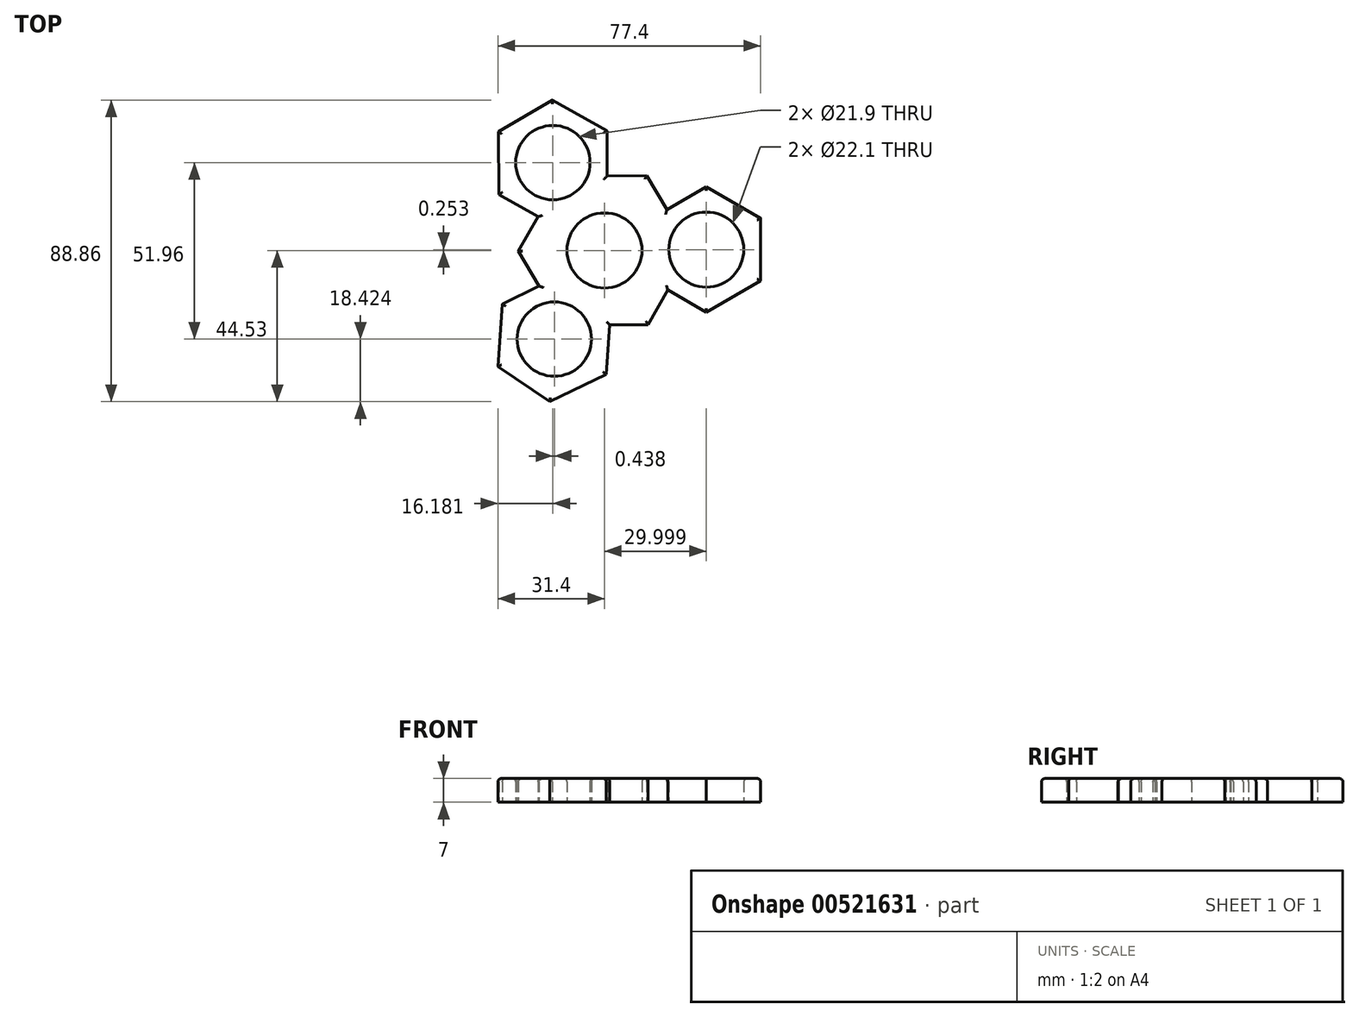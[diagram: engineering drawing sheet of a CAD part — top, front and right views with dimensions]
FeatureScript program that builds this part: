
annotation { "Feature Type Name" : "Feature", "Feature Type Description" : "" }
export const myFeature = defineFeature(function(context is Context, id is Id, definition is map)
    precondition{}
    {
        {
            var Q0;
            Q0=qCreatedBy(makeId("Top.planeOp"),FACE);
            var sketch = newSketch(context, id + "F0", { "sketchPlane" : qUnion([Q0])});
            skCircle(sketch, "E0", {"center": v(0, 0) * mm, "radius": 11.05 * mm});
            skCircle(sketch, "E1", {"center": v(-15.22, 25.85) * mm, "radius": 10.95 * mm});
            skCircle(sketch, "E2", {"center": v(-14.78, -26.1) * mm, "radius": 10.95 * mm});
            skCircle(sketch, "E3", {"center": v(30, 0.25) * mm, "radius": 11.05 * mm});
            skPoint(sketch, "E4.0.midPoint", {"position": v(5.37, -17.18) * mm});
            skPoint(sketch, "E5.0.midPoint", {"position": v(-24.47, 12.8) * mm});
            skLineSegment(sketch, "E6.0", {"start": v(-13.47, -7.68) * mm, "end": v(1.84, -18.03) * mm});
            skLineSegment(sketch, "E6.1", {"start": v(1.84, -18.03) * mm, "end": v(0.52, -36.46) * mm});
            skLineSegment(sketch, "E6.2", {"start": v(0.52, -36.46) * mm, "end": v(-16.1, -44.53) * mm});
            skLineSegment(sketch, "E6.3", {"start": v(-16.1, -44.53) * mm, "end": v(-31.4, -34.18) * mm});
            skLineSegment(sketch, "E6.4", {"start": v(-31.4, -34.18) * mm, "end": v(-30.08, -15.76) * mm});
            skLineSegment(sketch, "E6.5", {"start": v(-30.08, -15.76) * mm, "end": v(-13.47, -7.68) * mm});
            skPoint(sketch, "E6.0.midPoint", {"position": v(-5.82, -12.85) * mm});
            skLineSegment(sketch, "E7.0", {"start": v(14, -8.98) * mm, "end": v(14, 9.5) * mm});
            skLineSegment(sketch, "E7.1", {"start": v(14, 9.5) * mm, "end": v(30, 18.73) * mm});
            skLineSegment(sketch, "E7.2", {"start": v(30, 18.73) * mm, "end": v(46, 9.5) * mm});
            skLineSegment(sketch, "E7.3", {"start": v(46, 9.5) * mm, "end": v(46, -8.98) * mm});
            skLineSegment(sketch, "E7.4", {"start": v(46, -8.98) * mm, "end": v(30, -18.22) * mm});
            skLineSegment(sketch, "E7.5", {"start": v(30, -18.22) * mm, "end": v(14, -8.98) * mm});
            skPoint(sketch, "E7.0.midPoint", {"position": v(14, 0.25) * mm});
            skLineSegment(sketch, "E8.0", {"start": v(0.86, 16.75) * mm, "end": v(-15.06, 7.38) * mm});
            skLineSegment(sketch, "E8.1", {"start": v(-15.06, 7.38) * mm, "end": v(-31.14, 16.48) * mm});
            skLineSegment(sketch, "E8.2", {"start": v(-31.14, 16.48) * mm, "end": v(-31.3, 34.96) * mm});
            skLineSegment(sketch, "E8.3", {"start": v(-31.3, 34.96) * mm, "end": v(-15.37, 44.33) * mm});
            skLineSegment(sketch, "E8.4", {"start": v(-15.37, 44.33) * mm, "end": v(0.7, 35.23) * mm});
            skLineSegment(sketch, "E8.5", {"start": v(0.7, 35.23) * mm, "end": v(0.86, 16.75) * mm});
            skPoint(sketch, "E8.0.midPoint", {"position": v(-7.1, 12.06) * mm});
            skPoint(sketch, "E9.0.midPoint", {"position": v(-15.06, 7.38) * mm});
            skLineSegment(sketch, "E10", {"start": v(0, 0) * mm, "end": v(-15.22, 25.85) * mm});
            skLineSegment(sketch, "E11", {"start": v(0, 0) * mm, "end": v(-14.78, -26.1) * mm});
            skLineSegment(sketch, "E12", {"start": v(0, 0) * mm, "end": v(30, 0.25) * mm});
            skCircle(sketch, "E13.cCircle", {"center": v(0, 0) * mm, "radius": 21.95 * mm, "construction": true});
            skLineSegment(sketch, "E13.0", {"start": v(-12.86, 21.85) * mm, "end": v(12.49, 22.06) * mm});
            skLineSegment(sketch, "E13.1", {"start": v(12.49, 22.06) * mm, "end": v(25.35, 0.21) * mm});
            skLineSegment(sketch, "E13.2", {"start": v(25.35, 0.21) * mm, "end": v(12.86, -21.85) * mm});
            skLineSegment(sketch, "E13.3", {"start": v(12.86, -21.85) * mm, "end": v(-12.49, -22.06) * mm});
            skLineSegment(sketch, "E13.4", {"start": v(-12.49, -22.06) * mm, "end": v(-25.35, -0.21) * mm});
            skLineSegment(sketch, "E13.5", {"start": v(-25.35, -0.21) * mm, "end": v(-12.86, 21.85) * mm});
            skPoint(sketch, "E13.0.midPoint", {"position": v(-0.19, 21.95) * mm});
            skSolve(sketch);
        }
        {
            var Q0;
            {var subQ0=sQuery(id+"F0.wireOp",EDGE,"e9zcL3uG-clMW-CB6R-mPn1-NTrwoYadkIhf");var subQ1=sQuery(id+"F0.wireOp",EDGE,"E0");var subQ2=makeQuery(id+"F0.imprint","INTERSECT",VERTEX,{"derivedFrom":[subQ1,subQ0]});Q0=makeQuery(id+"F0.imprint","IMPRINT",FACE,{"disambiguationData":[TD([[makeQuery(id+"F0.imprint","IMPRINT",EDGE,{"disambiguationData":[TD([[subQ2,-1.0]])],"derivedFrom":subQ1}),-1.0]])]});}
            var Q1;
            Q1=makeQuery(id+"F0.imprint","IMPRINT",FACE,{"disambiguationData":[TD([[makeQuery(id+"F0.imprint","IMPRINT",EDGE,{"derivedFrom":sQuery(id+"F0.wireOp",EDGE,"E2")}),-1.0]])]});
            var Q2;
            {var subQ0=sQuery(id+"F0.wireOp",EDGE,"fM1NJ59R-5Gtm-2Vz8-hERX-S4Y3RQeVmU9U");var subQ1=sQuery(id+"F0.wireOp",EDGE,"EYICjCoY-6TXZ-VuYl-5S1G-jobRDzOFtBTO");var subQ2=makeQuery(id+"F0.imprint","INTERSECT",VERTEX,{"derivedFrom":[subQ1,subQ0]});Q2=makeQuery(id+"F0.imprint","IMPRINT",FACE,{"disambiguationData":[TD([[makeQuery(id+"F0.imprint","IMPRINT",EDGE,{"disambiguationData":[TD([[subQ2,-1.0]])],"derivedFrom":subQ1}),-1.0]])]});}
            var Q3;
            {var subQ0=sQuery(id+"F0.wireOp",EDGE,"oOAs71K8-LSWc-4CLp-Zzfn-c75iS4tNiohm");var subQ1=sQuery(id+"F0.wireOp",EDGE,"E0");var subQ2=makeQuery(id+"F0.imprint","INTERSECT",VERTEX,{"derivedFrom":[subQ1,subQ0]});Q3=makeQuery(id+"F0.imprint","IMPRINT",FACE,{"disambiguationData":[TD([[makeQuery(id+"F0.imprint","IMPRINT",EDGE,{"disambiguationData":[TD([[subQ2,1.0]])],"derivedFrom":subQ1}),-1.0]])]});}
            var Q4;
            {var subQ1=sQuery(id+"F0.wireOp",EDGE,"EYICjCoY-6TXZ-VuYl-5S1G-jobRDzOFtBTO");var subQ3=sQuery(id+"F0.wireOp",EDGE,"jgwlEjWp-sw9u-VY17-f9nH-SewB5XZ8HkPX");var subQ4=makeQuery(id+"F0.imprint","INTERSECT",VERTEX,{"derivedFrom":[subQ1,subQ3]});Q4=makeQuery(id+"F0.imprint","IMPRINT",FACE,{"disambiguationData":[TD([[makeQuery(id+"F0.imprint","IMPRINT",EDGE,{"disambiguationData":[TD([[subQ4,1.0]])],"derivedFrom":subQ3}),1.0]])]});}
            var Q5;
            {var subQ0=sQuery(id+"F0.wireOp",EDGE,"e9zcL3uG-clMW-CB6R-mPn1-NTrwoYadkIhf");var subQ1=sQuery(id+"F0.wireOp",EDGE,"E0");var subQ2=makeQuery(id+"F0.imprint","INTERSECT",VERTEX,{"derivedFrom":[subQ1,subQ0]});Q5=makeQuery(id+"F0.imprint","IMPRINT",FACE,{"disambiguationData":[TD([[makeQuery(id+"F0.imprint","IMPRINT",EDGE,{"disambiguationData":[TD([[subQ2,1.0]])],"derivedFrom":subQ1}),-1.0]])]});}
            var Q6;
            {var subQ1=sQuery(id+"F0.wireOp",EDGE,"EYICjCoY-6TXZ-VuYl-5S1G-jobRDzOFtBTO");var subQ3=sQuery(id+"F0.wireOp",EDGE,"oOAs71K8-LSWc-4CLp-Zzfn-c75iS4tNiohm");var subQ4=makeQuery(id+"F0.imprint","INTERSECT",VERTEX,{"derivedFrom":[subQ1,subQ3]});Q6=makeQuery(id+"F0.imprint","IMPRINT",FACE,{"disambiguationData":[TD([[makeQuery(id+"F0.imprint","IMPRINT",EDGE,{"disambiguationData":[TD([[subQ4,1.0]])],"derivedFrom":subQ3}),1.0]])]});}
            var Q7;
            Q7=makeQuery(id+"F0.imprint","IMPRINT",FACE,{"disambiguationData":[TD([[makeQuery(id+"F0.imprint","IMPRINT",EDGE,{"derivedFrom":sQuery(id+"F0.wireOp",EDGE,"E3")}),-1.0]])]});
            var Q8;
            Q8=makeQuery(id+"F0.imprint","IMPRINT",FACE,{"disambiguationData":[TD([[makeQuery(id+"F0.imprint","IMPRINT",EDGE,{"derivedFrom":sQuery(id+"F0.wireOp",EDGE,"E1")}),-1.0]])]});
            var Q9;
            {var subQ0=sQuery(id+"F0.wireOp",EDGE,"iWpcJYMW-lp7D-Rta9-vDUY-uTJnxPVIUKOB");var subQ1=sQuery(id+"F0.wireOp",EDGE,"EYICjCoY-6TXZ-VuYl-5S1G-jobRDzOFtBTO");var subQ2=makeQuery(id+"F0.imprint","INTERSECT",VERTEX,{"derivedFrom":[subQ1,subQ0]});Q9=makeQuery(id+"F0.imprint","IMPRINT",FACE,{"disambiguationData":[TD([[makeQuery(id+"F0.imprint","IMPRINT",EDGE,{"disambiguationData":[TD([[subQ2,-1.0]])],"derivedFrom":subQ1}),-1.0]])]});}
            var Q10;
            {var subQ0=sQuery(id+"F0.wireOp",EDGE,"nEZrQKPM-t3Dd-AM5R-DWg6-JUV7cxrYPtug");var subQ1=sQuery(id+"F0.wireOp",EDGE,"EYICjCoY-6TXZ-VuYl-5S1G-jobRDzOFtBTO");var subQ2=makeQuery(id+"F0.imprint","INTERSECT",VERTEX,{"derivedFrom":[subQ1,subQ0]});Q10=makeQuery(id+"F0.imprint","IMPRINT",FACE,{"disambiguationData":[TD([[makeQuery(id+"F0.imprint","IMPRINT",EDGE,{"disambiguationData":[TD([[subQ2,-1.0]])],"derivedFrom":subQ1}),-1.0]])]});}
            var Q11;
            {var subQ0=sQuery(id+"F0.wireOp",EDGE,"oOAs71K8-LSWc-4CLp-Zzfn-c75iS4tNiohm");var subQ1=sQuery(id+"F0.wireOp",EDGE,"EYICjCoY-6TXZ-VuYl-5S1G-jobRDzOFtBTO");var subQ2=makeQuery(id+"F0.imprint","INTERSECT",VERTEX,{"derivedFrom":[subQ1,subQ0]});Q11=makeQuery(id+"F0.imprint","IMPRINT",FACE,{"disambiguationData":[TD([[makeQuery(id+"F0.imprint","IMPRINT",EDGE,{"disambiguationData":[TD([[subQ2,1.0]])],"derivedFrom":subQ1}),1.0]])]});}
            var Q12;
            {var subQ0=sQuery(id+"F0.wireOp",EDGE,"jgwlEjWp-sw9u-VY17-f9nH-SewB5XZ8HkPX");var subQ1=sQuery(id+"F0.wireOp",EDGE,"EYICjCoY-6TXZ-VuYl-5S1G-jobRDzOFtBTO");var subQ2=makeQuery(id+"F0.imprint","INTERSECT",VERTEX,{"derivedFrom":[subQ1,subQ0]});Q12=makeQuery(id+"F0.imprint","IMPRINT",FACE,{"disambiguationData":[TD([[makeQuery(id+"F0.imprint","IMPRINT",EDGE,{"disambiguationData":[TD([[subQ2,1.0]])],"derivedFrom":subQ1}),1.0]])]});}
            var Q13;
            {var subQ1=sQuery(id+"F0.wireOp",EDGE,"EYICjCoY-6TXZ-VuYl-5S1G-jobRDzOFtBTO");var subQ3=sQuery(id+"F0.wireOp",EDGE,"e9zcL3uG-clMW-CB6R-mPn1-NTrwoYadkIhf");var subQ4=makeQuery(id+"F0.imprint","INTERSECT",VERTEX,{"derivedFrom":[subQ1,subQ3]});Q13=makeQuery(id+"F0.imprint","IMPRINT",FACE,{"disambiguationData":[TD([[makeQuery(id+"F0.imprint","IMPRINT",EDGE,{"disambiguationData":[TD([[subQ4,1.0]])],"derivedFrom":subQ3}),1.0]])]});}
            var Q14;
            {var subQ0=sQuery(id+"F0.wireOp",EDGE,"e9zcL3uG-clMW-CB6R-mPn1-NTrwoYadkIhf");var subQ1=sQuery(id+"F0.wireOp",EDGE,"EYICjCoY-6TXZ-VuYl-5S1G-jobRDzOFtBTO");var subQ2=makeQuery(id+"F0.imprint","INTERSECT",VERTEX,{"derivedFrom":[subQ1,subQ0]});Q14=makeQuery(id+"F0.imprint","IMPRINT",FACE,{"disambiguationData":[TD([[makeQuery(id+"F0.imprint","IMPRINT",EDGE,{"disambiguationData":[TD([[subQ2,1.0]])],"derivedFrom":subQ1}),1.0]])]});}
            var Q15;
            {var subQ0=sQuery(id+"F0.wireOp",EDGE,"z9qJ6aSi-ppxI-sIG3-XNC9-JwUbkRpWQMMj");var subQ1=sQuery(id+"F0.wireOp",EDGE,"EYICjCoY-6TXZ-VuYl-5S1G-jobRDzOFtBTO");var subQ2=makeQuery(id+"F0.imprint","INTERSECT",VERTEX,{"disambiguationData":[OD(0.0)],"derivedFrom":[subQ1,subQ0]});Q15=makeQuery(id+"F0.imprint","IMPRINT",FACE,{"disambiguationData":[TD([[makeQuery(id+"F0.imprint","IMPRINT",EDGE,{"disambiguationData":[TD([[subQ2,-1.0]])],"derivedFrom":subQ1}),1.0]])]});}
            var Q16;
            {var subQ0=sQuery(id+"F0.wireOp",EDGE,"o74pTpHK-wsrd-KW2E-Mtlw-4Mm4MKzACvNd");var subQ1=sQuery(id+"F0.wireOp",EDGE,"EYICjCoY-6TXZ-VuYl-5S1G-jobRDzOFtBTO");var subQ2=makeQuery(id+"F0.imprint","INTERSECT",VERTEX,{"disambiguationData":[OD(0.0)],"derivedFrom":[subQ1,subQ0]});Q16=makeQuery(id+"F0.imprint","IMPRINT",FACE,{"disambiguationData":[TD([[makeQuery(id+"F0.imprint","IMPRINT",EDGE,{"disambiguationData":[TD([[subQ2,-1.0]])],"derivedFrom":subQ1}),1.0]])]});}
            var Q17;
            {var subQ0=sQuery(id+"F0.wireOp",EDGE,"rjDIMbTK-I9fB-93H5-gbzg-zmOug2gslxki");var subQ1=sQuery(id+"F0.wireOp",EDGE,"EYICjCoY-6TXZ-VuYl-5S1G-jobRDzOFtBTO");var subQ2=makeQuery(id+"F0.imprint","INTERSECT",VERTEX,{"disambiguationData":[OD(0.0)],"derivedFrom":[subQ1,subQ0]});Q17=makeQuery(id+"F0.imprint","IMPRINT",FACE,{"disambiguationData":[TD([[makeQuery(id+"F0.imprint","IMPRINT",EDGE,{"disambiguationData":[TD([[subQ2,1.0]])],"derivedFrom":subQ1}),1.0]])]});}
            var Q18;
            {var subQ5=sQuery(id+"F0.wireOp",EDGE,"E7.2");Q18=makeQuery(id+"F0.imprint","IMPRINT",FACE,{"disambiguationData":[TD([[makeQuery(id+"F0.imprint","IMPRINT",EDGE,{"derivedFrom":subQ5}),-1.0]])]});}
            var Q19;
            Q19=makeQuery(id+"F0.imprint","IMPRINT",FACE,{"disambiguationData":[TD([[makeQuery(id+"F0.imprint","IMPRINT",EDGE,{"derivedFrom":sQuery(id+"F0.wireOp",EDGE,"E0")}),-1.0]])]});
            var Q20;
            {var subQ1=sQuery(id+"F0.wireOp",EDGE,"E8.0");Q20=makeQuery(id+"F0.imprint","IMPRINT",FACE,{"disambiguationData":[TD([[makeQuery(id+"F0.imprint","IMPRINT",EDGE,{"derivedFrom":subQ1}),-1.0]])]});}
            var Q21;
            {var subQ2=sQuery(id+"F0.wireOp",EDGE,"E4.1");Q21=makeQuery(id+"F0.imprint","IMPRINT",FACE,{"disambiguationData":[TD([[makeQuery(id+"F0.imprint","IMPRINT",EDGE,{"derivedFrom":subQ2}),-1.0]])]});}
            var Q22;
            {var subQ0=sQuery(id+"F0.wireOp",EDGE,"E8.1");Q22=makeQuery(id+"F0.imprint","IMPRINT",FACE,{"disambiguationData":[TD([[makeQuery(id+"F0.imprint","IMPRINT",EDGE,{"derivedFrom":subQ0}),-1.0]])]});}
            var Q23;
            {var subQ5=sQuery(id+"F0.wireOp",EDGE,"E6.1");Q23=makeQuery(id+"F0.imprint","IMPRINT",FACE,{"disambiguationData":[TD([[makeQuery(id+"F0.imprint","IMPRINT",EDGE,{"derivedFrom":subQ5}),-1.0]])]});}
            var Q24;
            {var subQ0=sQuery(id+"F0.wireOp",EDGE,"E8.2");Q24=makeQuery(id+"F0.imprint","IMPRINT",FACE,{"disambiguationData":[TD([[makeQuery(id+"F0.imprint","IMPRINT",EDGE,{"derivedFrom":subQ0}),-1.0]])]});}
            var Q25;
            {var subQ5=sQuery(id+"F0.wireOp",EDGE,"E6.2");Q25=makeQuery(id+"F0.imprint","IMPRINT",FACE,{"disambiguationData":[TD([[makeQuery(id+"F0.imprint","IMPRINT",EDGE,{"derivedFrom":subQ5}),-1.0]])]});}
            extrude(context, id + "F1", {"entities" : qUnion([Q0, Q1, Q2, Q3, Q4, Q5, Q6, Q7, Q8, Q9, Q10, Q11, Q12, Q13, Q14, Q15, Q16, Q17, Q18, Q19, Q20, Q21, Q22, Q23, Q24, Q25]), "depth" : 7 * mm, "offsetDistance" : 25 * mm});
        }
        {
            var Q0;
            Q0=makeQuery(id+"F1.opExtrude","CAP_FACE",FACE,{"disambiguationData":[OSD([sQuery(id+"F0.wireOp",EDGE,"E0"),sQuery(id+"F0.wireOp",EDGE,"E1"),sQuery(id+"F0.wireOp",EDGE,"E2"),sQuery(id+"F0.wireOp",EDGE,"E3"),sQuery(id+"F0.wireOp",EDGE,"z9qJ6aSi-ppxI-sIG3-XNC9-JwUbkRpWQMMj"),sQuery(id+"F0.wireOp",EDGE,"o74pTpHK-wsrd-KW2E-Mtlw-4Mm4MKzACvNd"),sQuery(id+"F0.wireOp",EDGE,"rjDIMbTK-I9fB-93H5-gbzg-zmOug2gslxki"),sQuery(id+"F0.wireOp",EDGE,"iWpcJYMW-lp7D-Rta9-vDUY-uTJnxPVIUKOB"),sQuery(id+"F0.wireOp",EDGE,"fM1NJ59R-5Gtm-2Vz8-hERX-S4Y3RQeVmU9U"),sQuery(id+"F0.wireOp",EDGE,"nEZrQKPM-t3Dd-AM5R-DWg6-JUV7cxrYPtug")])],"isStart":false});
            fillet(context, id + "F2", {"entities" : qUnion([Q0]), "radius" : 1 * mm, "tangentPropagation" : true, "allowEdgeOverflow" : false});
        }
    });
